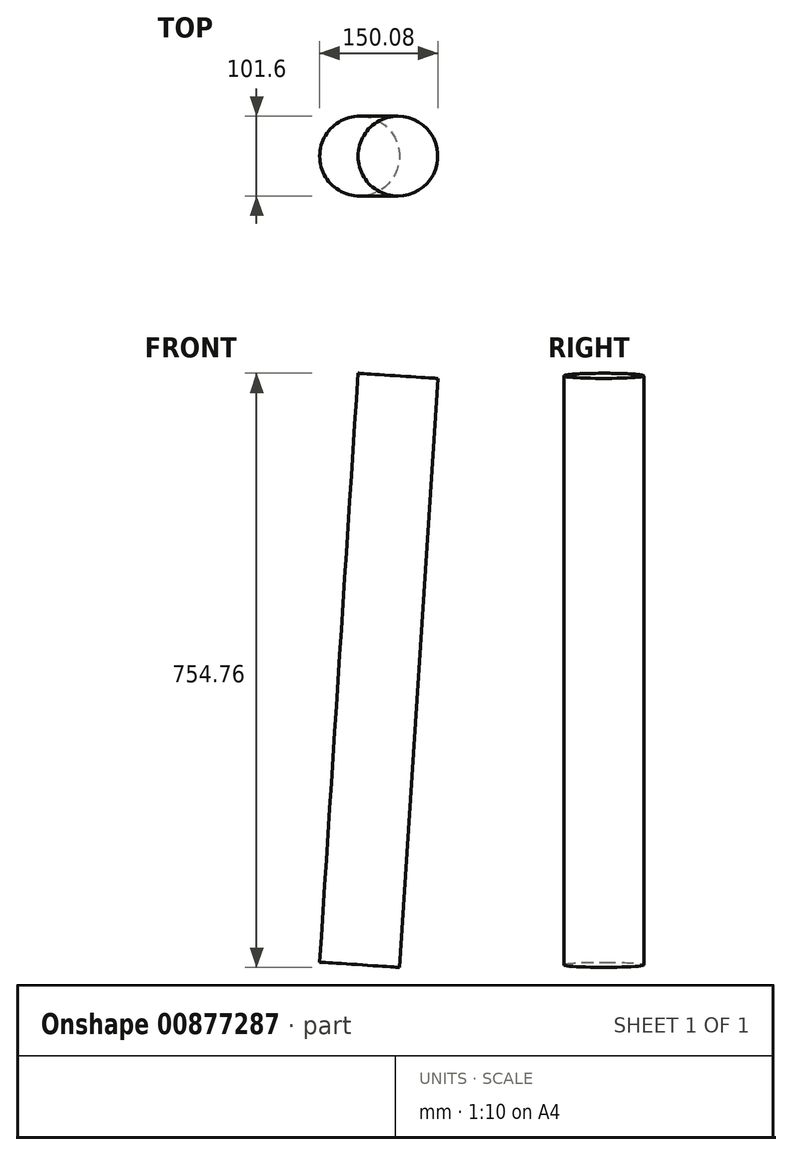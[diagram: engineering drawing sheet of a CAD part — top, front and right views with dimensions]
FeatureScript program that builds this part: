
annotation { "Feature Type Name" : "Feature", "Feature Type Description" : "" }
export const myFeature = defineFeature(function(context is Context, id is Id, definition is map)
    precondition{}
    {
        {
            var Q0;
            Q0=qCreatedBy(makeId("Front.planeOp"),FACE);
            var sketch = newSketch(context, id + "F0", { "sketchPlane" : qUnion([Q0])});
            skCircle(sketch, "E0", {"center": v(-120.6, -526) * mm, "radius": 107.1 * mm});
            skLineSegment(sketch, "E1", {"start": v(0, 0) * mm, "end": v(-136.64, 71.08) * mm});
            skLineSegment(sketch, "E2", {"start": v(-136.64, 71.08) * mm, "end": v(-79.03, -427.3) * mm});
            skLineSegment(sketch, "E3", {"start": v(0, 0) * mm, "end": v(205.83, -64.84) * mm});
            skLineSegment(sketch, "E4", {"start": v(201.3, -134.54) * mm, "end": v(152.6, -882.7) * mm});
            skLineSegment(sketch, "E5", {"start": v(201.3, -134.54) * mm, "end": v(205.83, -64.84) * mm});
            skCircle(sketch, "E6", {"center": v(0, 0) * mm, "radius": 31.75 * mm});
            skSolve(sketch);
        }
        {
            var Q0;
            Q0=sQuery(id+"F0.wireOp",EDGE,"E4");
            var Q1;
            Q1=qBodyType(qCreatedBy(id+"F2",EDGE),BodyType.WIRE);
            cPlane(context, id + "F1", {"entities" : qUnion([Q0, Q1]), "cplaneType" : CPlaneType.MID_PLANE, "offset" : 25 * mm, "width" : 150 * mm, "height" : 150 * mm});
        }
        {
            var Q0;
            Q0=qCreatedBy(id+"F1.planeOp",FACE);
            var sketch = newSketch(context, id + "F2", { "sketchPlane" : qUnion([Q0])});
            skCircle(sketch, "E7", {"center": v(209.6, 0) * mm, "radius": 50.8 * mm});
            skSolve(sketch);
        }
        {
            var Q0;
            Q0=makeQuery(id+"F2.imprint","IMPRINT",FACE,{"disambiguationData":[TD([[makeQuery(id+"F2.imprint","IMPRINT",EDGE,{"derivedFrom":sQuery(id+"F2.wireOp",EDGE,"E7")}),1.0]])]});
            var Q1;
            Q1=sQuery(id+"F0.wireOp",EDGE,"E4");
            sweep(context, id + "F3", {"profiles" : qUnion([Q0]), "path" : qUnion([Q1])});
        }
    });
